# Revit family: FantiniCosmi_BIM_AP20058
name_source: partatom
category: Modelli generici
units: mm (PartAtom-declared; Revit-internal decimal feet)

## family parameters
Basato su piano di lavoro = No
Condiviso = No
Punto di calcolo locali = No
Può ospitare armatura = No
Quota connettore circolare = Usa diametro
Sempre verticale = Sì
Taglio con vuoti quando caricato = No
Tipo di parte = Normale

## types (1)
- Standard
    Average Sound Pressure (Lp) 1Mt = 51.9 dB(A)
    Average Sound Pressure (Lp) 3Mt = 44.4
    Descrizione = HRP DOMO 50 V
    Fan Number = 2
    Filteration Class = ePM1 70%
    Heat Recovery Efficiency = 84.5
    Max Flow = 475 mc/h
    Part Number = AP20058
    Pressure = 100 Pa
    Prospetto di default = 0 mm  [stored 0 ft]
    Sound Power (Lw) from body = 66 dB(A)
    Sound Power (Lw) from channels = 73 dB(A)
    Weight = 65 Kg

note: [stored X ft] marks values corroborated as IEEE doubles in the binary element streams (Revit-internal decimal feet)

## geometry (parser evidence)
native form markers: Sweep x3
no freeform markers — native parametric forms only
